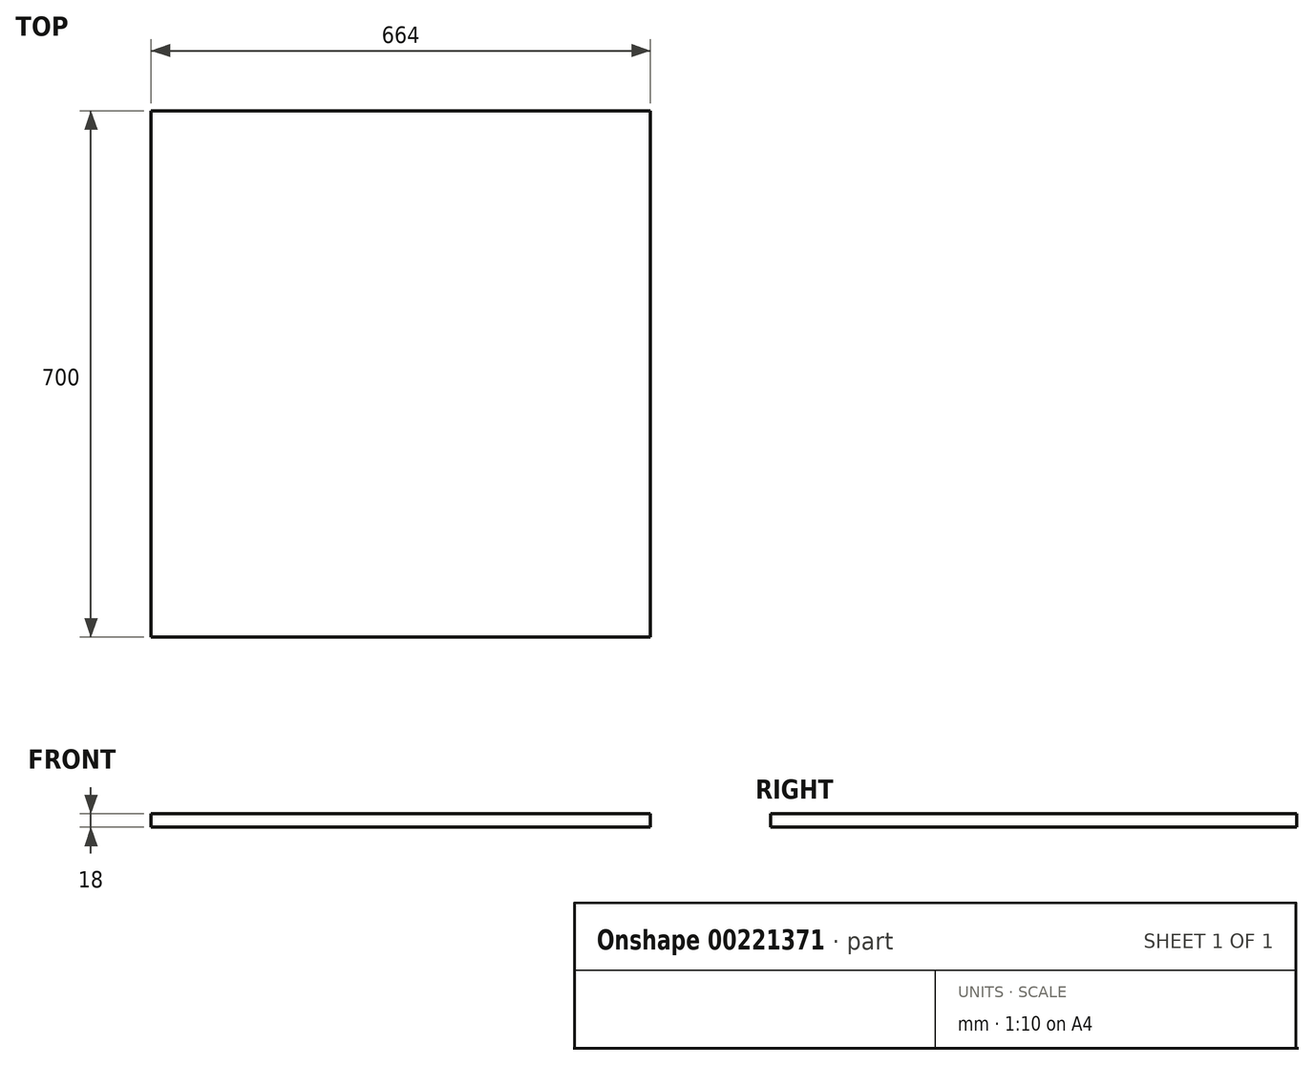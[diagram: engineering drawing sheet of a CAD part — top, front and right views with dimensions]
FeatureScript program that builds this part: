
annotation { "Feature Type Name" : "Feature", "Feature Type Description" : "" }
export const myFeature = defineFeature(function(context is Context, id is Id, definition is map)
    precondition{}
    {
        {
            var Q0;
            Q0=qCreatedBy(makeId("Top.planeOp"),FACE);
            var sketch = newSketch(context, id + "F0", { "sketchPlane" : qUnion([Q0])});
            skLineSegment(sketch, "E0.bottom", {"start": v(332, -350) * mm, "end": v(-332, -350) * mm});
            skLineSegment(sketch, "E0.top", {"start": v(332, 350) * mm, "end": v(-332, 350) * mm});
            skLineSegment(sketch, "E0.left", {"start": v(332, -350) * mm, "end": v(332, 350) * mm});
            skLineSegment(sketch, "E0.right", {"start": v(-332, -350) * mm, "end": v(-332, 350) * mm});
            skPoint(sketch, "E0.middle", {"position": v(0, 0) * mm});
            skSolve(sketch);
        }
        {
            var Q0;
            Q0 = qSketchRegion(id + "F0", true);
            extrude(context, id + "F1", {"entities" : qUnion([Q0]), "depth" : 18 * mm});
        }
    });
